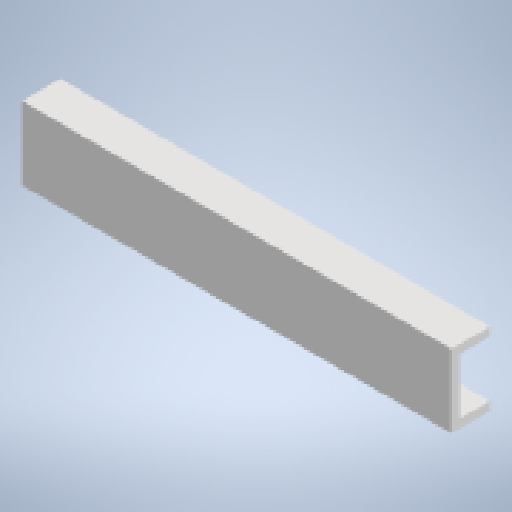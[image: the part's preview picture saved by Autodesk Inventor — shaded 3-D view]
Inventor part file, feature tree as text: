
AUTODESK INVENTOR PART (.ipt)
format: ipt  version: 2024.2 (Build 282272000, 272)  size: 131,072 bytes
history: native  units: mm
features: extrude x1, sketch x1
ambient origin geometry x8: Origin, YZ Plane, XZ Plane, XY Plane, X Axis, Y Axis, Z Axis, Center Point
bodies: Solid1 (feature_tree)
feature tree (2):
  extrude  "Extrusion1"  Depth=17.0mm
  sketch  "Sketch1"  dims[d0=9.0mm d1=17.0mm d3=13.0mm d4=2.0mm d5=2.0mm d6=2.0mm d7=100.0mm d8=0.0mm]
